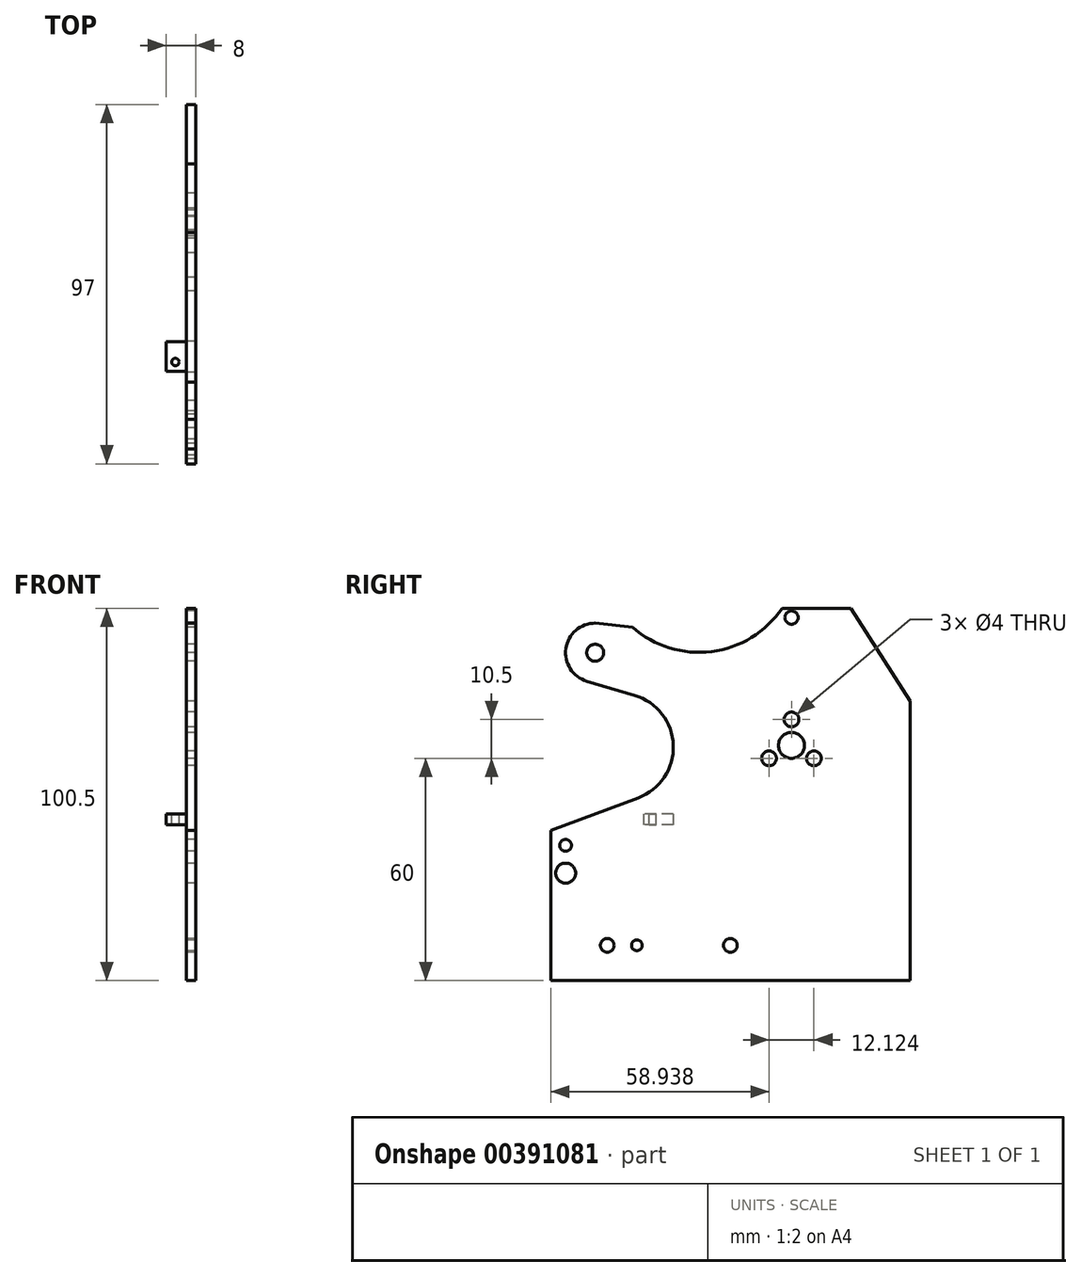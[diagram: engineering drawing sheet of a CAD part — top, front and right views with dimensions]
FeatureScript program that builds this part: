
annotation { "Feature Type Name" : "Feature", "Feature Type Description" : "" }
export const myFeature = defineFeature(function(context is Context, id is Id, definition is map)
    precondition{}
    {
        {
            var Q0;
            Q0=qCreatedBy(makeId("Right.planeOp"),FACE);
            var sketch = newSketch(context, id + "F0", { "sketchPlane" : qUnion([Q0])});
            skLineSegment(sketch, "E0.bottom", {"start": v(0, 0) * mm, "end": v(97, 0) * mm});
            skLineSegment(sketch, "E0.top", {"start": v(0, 100.5) * mm, "end": v(17.56, 100.5) * mm});
            skLineSegment(sketch, "E0.left", {"start": v(0, 0) * mm, "end": v(0, 100.5) * mm});
            skLineSegment(sketch, "E0.right", {"start": v(97, 0) * mm, "end": v(97, 75.5) * mm});
            skPoint(sketch, "E1", {"position": v(18.5, 63) * mm});
            skArc(sketch, "E2", {"start": v(23.61, 49.32) * mm, "mid": v(33.1, 63.5) * mm, "end": v(22.65, 77) * mm});
            skPoint(sketch, "E3", {"position": v(0, 40.5) * mm});
            skLineSegment(sketch, "E4", {"start": v(0, 40.5) * mm, "end": v(23.61, 49.32) * mm});
            skPoint(sketch, "E5", {"position": v(12, 88.5) * mm});
            skArc(sketch, "E6", {"start": v(13.75, 96.3) * mm, "mid": v(4.26, 90.51) * mm, "end": v(9.73, 80.83) * mm});
            skLineSegment(sketch, "E7", {"start": v(9.73, 80.83) * mm, "end": v(22.65, 77) * mm});
            skPoint(sketch, "E8", {"position": v(12, 96.5) * mm});
            skLineSegment(sketch, "E9", {"start": v(12, 96.5) * mm, "end": v(22.06, 95.39) * mm});
            skArc(sketch, "E10", {"start": v(22.06, 95.39) * mm, "mid": v(43.4, 88.81) * mm, "end": v(62.44, 100.5) * mm});
            skLineSegment(sketch, "E11.trimOffspring", {"start": v(62.44, 100.5) * mm, "end": v(81, 100.5) * mm});
            skPoint(sketch, "E12", {"position": v(81, 100.5) * mm});
            skPoint(sketch, "E13", {"position": v(97, 75.5) * mm});
            skLineSegment(sketch, "E14", {"start": v(81, 100.5) * mm, "end": v(97, 75.5) * mm});
            skSolve(sketch);
        }
        {
            var Q0;
            Q0=qCreatedBy(makeId("Right.planeOp"),FACE);
            var sketch = newSketch(context, id + "F1", { "sketchPlane" : qUnion([Q0])});
            skLineSegment(sketch, "E15", {"start": v(48.5, 0) * mm, "end": v(48.5, 9.5) * mm, "construction": true});
            skCircle(sketch, "E16", {"center": v(48.5, 9.5) * mm, "radius": 1.85 * mm});
            skCircle(sketch, "E17", {"center": v(15.25, 9.5) * mm, "radius": 1.85 * mm});
            skCircle(sketch, "E18", {"center": v(23.25, 9.5) * mm, "radius": 1.45 * mm});
            skCircle(sketch, "E19.MirrorC", {"center": v(73.75, 9.5) * mm, "radius": 1.45 * mm});
            skCircle(sketch, "E20.MirrorC", {"center": v(81.75, 9.5) * mm, "radius": 1.85 * mm});
            skCircle(sketch, "E21", {"center": v(65, 63.5) * mm, "radius": 3.5 * mm});
            skCircle(sketch, "E22", {"center": v(65, 70.5) * mm, "radius": 2 * mm});
            skCircle(sketch, "E23.1.0", {"center": v(58.94, 60) * mm, "radius": 2 * mm});
            skCircle(sketch, "E23.2.0", {"center": v(71.06, 60) * mm, "radius": 2 * mm});
            skCircle(sketch, "E24", {"center": v(4, 29) * mm, "radius": 2.7 * mm});
            skLineSegment(sketch, "E25", {"start": v(4, 29) * mm, "end": v(0, 29) * mm, "construction": true});
            skCircle(sketch, "E26", {"center": v(4, 36.5) * mm, "radius": 1.6 * mm});
            skCircle(sketch, "E27.MirrorC", {"center": v(4, 21.5) * mm, "radius": 1.6 * mm});
            skPoint(sketch, "E28.0", {"position": v(12, 88.5) * mm});
            skCircle(sketch, "E29", {"center": v(12, 88.5) * mm, "radius": 2.3 * mm});
            skCircle(sketch, "E30", {"center": v(65, 98) * mm, "radius": 1.8 * mm});
            skSolve(sketch);
        }
        {
            var Q0;
            {var subQ7=sQuery(id+"F0.wireOp",EDGE,"E0.bottom");Q0=makeQuery(id+"F0.imprint","IMPRINT",FACE,{"disambiguationData":[TD([[makeQuery(id+"F0.imprint","IMPRINT",EDGE,{"derivedFrom":subQ7}),1.0]])]});}
            extrude(context, id + "F2", {"entities" : qUnion([Q0]), "depth" : 2.5 * mm, "offsetDistance" : 25 * mm});
        }
        {
            var Q0;
            Q0=makeQuery(id+"F1.imprint","IMPRINT",FACE,{"disambiguationData":[TD([[makeQuery(id+"F1.imprint","IMPRINT",EDGE,{"derivedFrom":sQuery(id+"F1.wireOp",EDGE,"E30")}),1.0]])]});
            var Q1;
            Q1=makeQuery(id+"F1.imprint","IMPRINT",FACE,{"disambiguationData":[TD([[makeQuery(id+"F1.imprint","IMPRINT",EDGE,{"derivedFrom":sQuery(id+"F1.wireOp",EDGE,"E22")}),1.0]])]});
            var Q2;
            Q2=makeQuery(id+"F1.imprint","IMPRINT",FACE,{"disambiguationData":[TD([[makeQuery(id+"F1.imprint","IMPRINT",EDGE,{"derivedFrom":sQuery(id+"F1.wireOp",EDGE,"E21")}),1.0]])]});
            var Q3;
            Q3=makeQuery(id+"F1.imprint","IMPRINT",FACE,{"disambiguationData":[TD([[makeQuery(id+"F1.imprint","IMPRINT",EDGE,{"derivedFrom":sQuery(id+"F1.wireOp",EDGE,"E23.1.0")}),1.0]])]});
            var Q4;
            Q4=makeQuery(id+"F1.imprint","IMPRINT",FACE,{"disambiguationData":[TD([[makeQuery(id+"F1.imprint","IMPRINT",EDGE,{"derivedFrom":sQuery(id+"F1.wireOp",EDGE,"E23.2.0")}),1.0]])]});
            var Q5;
            Q5=makeQuery(id+"F1.imprint","IMPRINT",FACE,{"disambiguationData":[TD([[makeQuery(id+"F1.imprint","IMPRINT",EDGE,{"derivedFrom":sQuery(id+"F1.wireOp",EDGE,"E29")}),1.0]])]});
            var Q6;
            Q6=makeQuery(id+"F1.imprint","IMPRINT",FACE,{"disambiguationData":[TD([[makeQuery(id+"F1.imprint","IMPRINT",EDGE,{"derivedFrom":sQuery(id+"F1.wireOp",EDGE,"E26")}),1.0]])]});
            var Q7;
            Q7=makeQuery(id+"F1.imprint","IMPRINT",FACE,{"disambiguationData":[TD([[makeQuery(id+"F1.imprint","IMPRINT",EDGE,{"derivedFrom":sQuery(id+"F1.wireOp",EDGE,"E24")}),1.0]])]});
            var Q8;
            Q8=makeQuery(id+"F1.imprint","IMPRINT",FACE,{"disambiguationData":[TD([[makeQuery(id+"F1.imprint","IMPRINT",EDGE,{"derivedFrom":sQuery(id+"F1.wireOp",EDGE,"E27.MirrorC")}),-1.0]])]});
            var Q9;
            Q9=makeQuery(id+"F1.imprint","IMPRINT",FACE,{"disambiguationData":[TD([[makeQuery(id+"F1.imprint","IMPRINT",EDGE,{"derivedFrom":sQuery(id+"F1.wireOp",EDGE,"E17")}),1.0]])]});
            var Q10;
            Q10=makeQuery(id+"F1.imprint","IMPRINT",FACE,{"disambiguationData":[TD([[makeQuery(id+"F1.imprint","IMPRINT",EDGE,{"derivedFrom":sQuery(id+"F1.wireOp",EDGE,"E18")}),1.0]])]});
            var Q11;
            Q11=makeQuery(id+"F1.imprint","IMPRINT",FACE,{"disambiguationData":[TD([[makeQuery(id+"F1.imprint","IMPRINT",EDGE,{"derivedFrom":sQuery(id+"F1.wireOp",EDGE,"E16")}),1.0]])]});
            var Q12;
            Q12=makeQuery(id+"F1.imprint","IMPRINT",FACE,{"disambiguationData":[TD([[makeQuery(id+"F1.imprint","IMPRINT",EDGE,{"derivedFrom":sQuery(id+"F1.wireOp",EDGE,"E20.MirrorC")}),-1.0]])]});
            var Q13;
            Q13=makeQuery(id+"F1.imprint","IMPRINT",FACE,{"disambiguationData":[TD([[makeQuery(id+"F1.imprint","IMPRINT",EDGE,{"derivedFrom":sQuery(id+"F1.wireOp",EDGE,"E19.MirrorC")}),-1.0]])]});
            extrude(context, id + "F3", {"entities" : qUnion([Q0, Q1, Q2, Q3, Q4, Q5, Q6, Q7, Q8, Q9, Q10, Q11, Q12, Q13]), "operationType" : NewBodyOperationType.REMOVE, "endBound" : BoundingType.THROUGH_ALL, "depth" : 25 * mm, "offsetDistance" : 25 * mm});
        }
        {
            var Q0;
            Q0=qCreatedBy(makeId("Right.planeOp"),FACE);
            var sketch = newSketch(context, id + "F4", { "sketchPlane" : qUnion([Q0])});
            skLineSegment(sketch, "E31.bottom", {"start": v(33, 45) * mm, "end": v(25, 45) * mm});
            skLineSegment(sketch, "E31.top", {"start": v(33, 42) * mm, "end": v(25, 42) * mm});
            skLineSegment(sketch, "E31.left", {"start": v(33, 45) * mm, "end": v(33, 42) * mm});
            skLineSegment(sketch, "E31.right", {"start": v(25, 45) * mm, "end": v(25, 42) * mm});
            skSolve(sketch);
        }
        {
            var Q0;
            Q0=makeQuery(id+"F4.imprint","IMPRINT",FACE,{"disambiguationData":[TD([[makeQuery(id+"F4.imprint","IMPRINT",EDGE,{"derivedFrom":sQuery(id+"F4.wireOp",EDGE,"E31.bottom")}),1.0]])]});
            extrude(context, id + "F5", {"entities" : qUnion([Q0]), "operationType" : NewBodyOperationType.ADD, "oppositeDirection" : true, "depth" : 5.5 * mm, "offsetDistance" : 25 * mm});
        }
        {
            var Q0;
            Q0=makeQuery(id+"F5.opExtrude","SWEPT_FACE",FACE,{"disambiguationData":[OSD([sQuery(id+"F4.wireOp",EDGE,"E31.bottom")])]});
            var sketch = newSketch(context, id + "F6", { "sketchPlane" : qUnion([Q0])});
            skCircle(sketch, "E32", {"center": v(-3, 27.5) * mm, "radius": 1 * mm});
            skSolve(sketch);
        }
        {
            var Q0;
            Q0=makeQuery(id+"F6.imprint","IMPRINT",FACE,{"disambiguationData":[TD([[makeQuery(id+"F6.imprint","IMPRINT",EDGE,{"derivedFrom":sQuery(id+"F6.wireOp",EDGE,"E32")}),1.0]])]});
            extrude(context, id + "F7", {"entities" : qUnion([Q0]), "operationType" : NewBodyOperationType.REMOVE, "endBound" : BoundingType.THROUGH_ALL, "oppositeDirection" : true, "depth" : 25 * mm, "offsetDistance" : 25 * mm});
        }
    });
